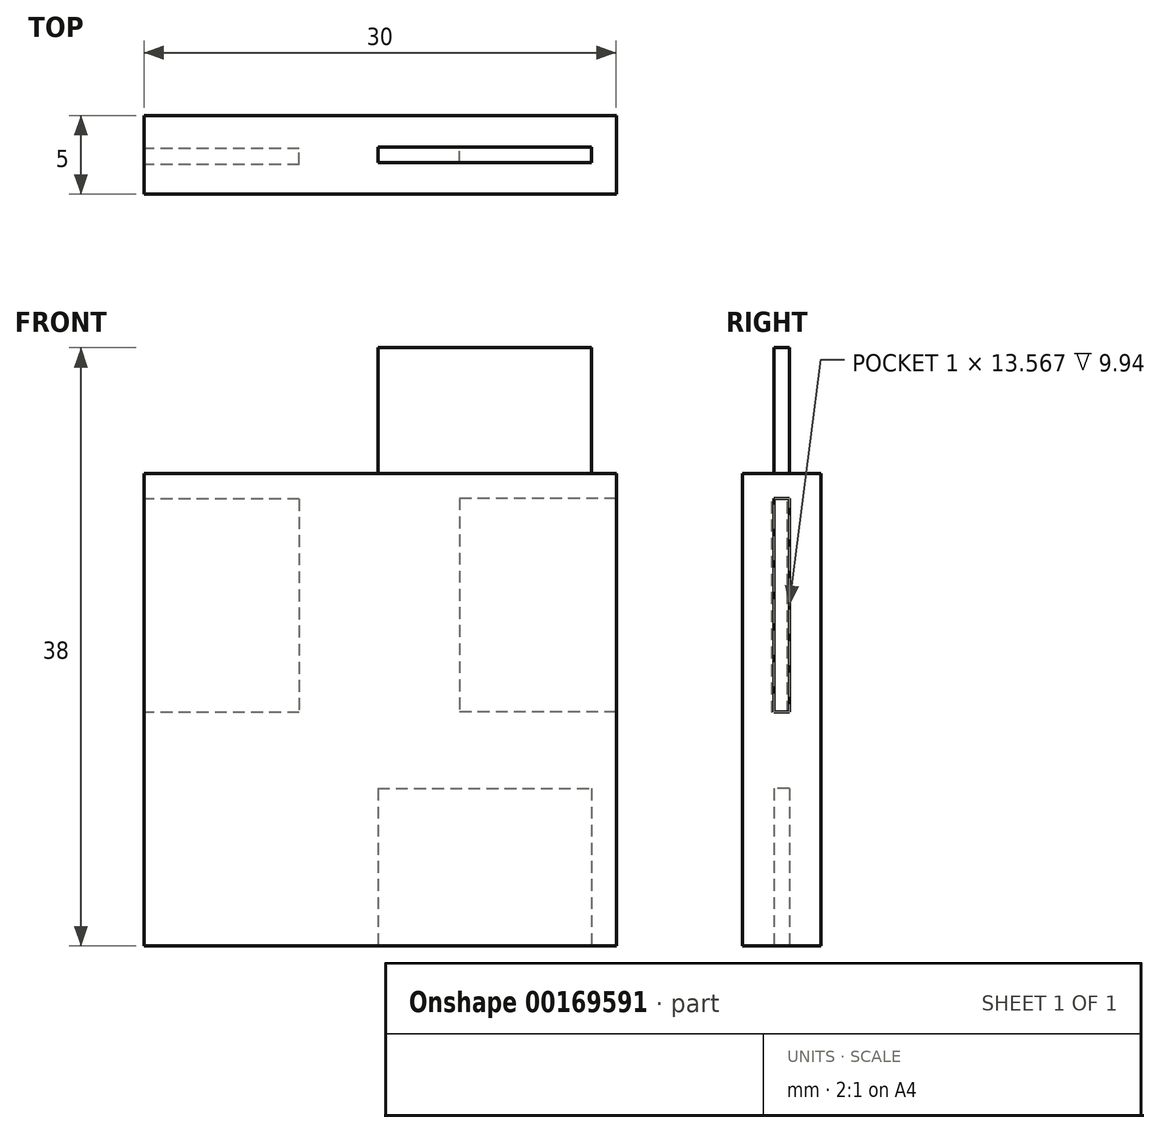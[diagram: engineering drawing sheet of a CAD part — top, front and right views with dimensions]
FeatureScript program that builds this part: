
annotation { "Feature Type Name" : "Feature", "Feature Type Description" : "" }
export const myFeature = defineFeature(function(context is Context, id is Id, definition is map)
    precondition{}
    {
        {
            var Q0;
            Q0=qCreatedBy(makeId("Top.planeOp"),FACE);
            var sketch = newSketch(context, id + "F0", { "sketchPlane" : qUnion([Q0])});
            skLineSegment(sketch, "E0.bottom", {"start": v(-14.86, -2.76) * mm, "end": v(15.14, -2.76) * mm});
            skLineSegment(sketch, "E0.top", {"start": v(-14.86, -7.76) * mm, "end": v(15.14, -7.76) * mm});
            skLineSegment(sketch, "E0.left", {"start": v(-14.86, -2.76) * mm, "end": v(-14.86, -7.76) * mm});
            skLineSegment(sketch, "E0.right", {"start": v(15.14, -2.76) * mm, "end": v(15.14, -7.76) * mm});
            skSolve(sketch);
        }
        {
            var Q0;
            Q0 = qSketchRegion(id + "F0", true);
            extrude(context, id + "F1", {"entities" : qUnion([Q0]), "depth" : 30 * mm, "offsetDistance" : 25 * mm});
        }
        {
            var Q0;
            Q0=qCreatedBy(makeId("Top.planeOp"),FACE);
            var sketch = newSketch(context, id + "F2", { "sketchPlane" : qUnion([Q0])});
            skLineSegment(sketch, "E1.bottom", {"start": v(0, -4.76) * mm, "end": v(13.57, -4.76) * mm});
            skLineSegment(sketch, "E1.top", {"start": v(0, -5.76) * mm, "end": v(13.57, -5.76) * mm});
            skLineSegment(sketch, "E1.left", {"start": v(0, -4.76) * mm, "end": v(0, -5.76) * mm});
            skLineSegment(sketch, "E1.right", {"start": v(13.57, -4.76) * mm, "end": v(13.57, -5.76) * mm});
            skSolve(sketch);
        }
        {
            var Q0;
            Q0 = qSketchRegion(id + "F2", true);
            extrude(context, id + "F3", {"entities" : qUnion([Q0]), "operationType" : NewBodyOperationType.REMOVE, "depth" : 10 * mm, "offsetDistance" : 25 * mm});
        }
        {
            var Q0;
            Q0=qCreatedBy(makeId("Top.planeOp"),FACE);
            var sketch = newSketch(context, id + "F4", { "sketchPlane" : qUnion([Q0])});
            skLineSegment(sketch, "E2.bottom", {"start": v(0, -4.76) * mm, "end": v(13.57, -4.76) * mm});
            skLineSegment(sketch, "E2.top", {"start": v(0, -5.76) * mm, "end": v(13.57, -5.76) * mm});
            skLineSegment(sketch, "E2.left", {"start": v(0, -4.76) * mm, "end": v(0, -5.76) * mm});
            skLineSegment(sketch, "E2.right", {"start": v(13.57, -4.76) * mm, "end": v(13.57, -5.76) * mm});
            skSolve(sketch);
        }
        {
            var Q0;
            Q0 = qSketchRegion(id + "F4", true);
            extrude(context, id + "F5", {"entities" : qUnion([Q0]), "depth" : 8 * mm, "offsetDistance" : 25 * mm});
        }
        {
            var Q0;
            Q0=makeQuery(id+"F5.opExtrude","SWEPT_BODY",BODY,{"disambiguationData":[OSD([sQuery(id+"F4.wireOp",EDGE,"E2.bottom"),sQuery(id+"F4.wireOp",EDGE,"E2.top"),sQuery(id+"F4.wireOp",EDGE,"E2.left"),sQuery(id+"F4.wireOp",EDGE,"E2.right")])]});
            transform(context, id + "F6", {"entities" : qUnion([Q0]), "transformType" : TransformType.TRANSLATION_3D, "dx" : 0 * mm, "dy" : 0 * mm, "dz" : 30 * mm, "makeCopy" : false});
        }
        {
            var Q0;
            Q0=qCreatedBy(makeId("Right.planeOp"),FACE);
            var sketch = newSketch(context, id + "F7", { "sketchPlane" : qUnion([Q0])});
            skLineSegment(sketch, "E3.bottom", {"start": v(-5.87, 31.97) * mm, "end": v(-4.87, 31.97) * mm});
            skLineSegment(sketch, "E3.top", {"start": v(-5.87, 18.4) * mm, "end": v(-4.87, 18.4) * mm});
            skLineSegment(sketch, "E3.left", {"start": v(-5.87, 31.97) * mm, "end": v(-5.87, 18.4) * mm});
            skLineSegment(sketch, "E3.right", {"start": v(-4.87, 31.97) * mm, "end": v(-4.87, 18.4) * mm});
            skSolve(sketch);
        }
        {
            var Q0;
            Q0 = qSketchRegion(id + "F7", true);
            extrude(context, id + "F8", {"entities" : qUnion([Q0]), "depth" : 10 * mm, "offsetDistance" : 25 * mm});
        }
        {
            var Q0;
            Q0=makeQuery(id+"F8.opExtrude","SWEPT_BODY",BODY,{"disambiguationData":[OSD([sQuery(id+"F7.wireOp",EDGE,"E3.bottom"),sQuery(id+"F7.wireOp",EDGE,"E3.top"),sQuery(id+"F7.wireOp",EDGE,"E3.left"),sQuery(id+"F7.wireOp",EDGE,"E3.right")])]});
            transform(context, id + "F9", {"entities" : qUnion([Q0]), "transformType" : TransformType.TRANSLATION_3D, "dx" : -15 * mm, "dy" : 0 * mm, "dz" : -3.57 * mm, "makeCopy" : false});
        }
        {
            var Q0;
            Q0=makeQuery(id+"F8.opExtrude","SWEPT_BODY",BODY,{"disambiguationData":[OSD([sQuery(id+"F7.wireOp",EDGE,"E3.bottom"),sQuery(id+"F7.wireOp",EDGE,"E3.top"),sQuery(id+"F7.wireOp",EDGE,"E3.left"),sQuery(id+"F7.wireOp",EDGE,"E3.right")])]});
            var Q1;
            Q1=makeQuery(id+"F1.opExtrude","SWEPT_BODY",BODY,{"disambiguationData":[OSD([sQuery(id+"F0.wireOp",EDGE,"E0.bottom"),sQuery(id+"F0.wireOp",EDGE,"E0.top"),sQuery(id+"F0.wireOp",EDGE,"E0.left"),sQuery(id+"F0.wireOp",EDGE,"E0.right")])]});
            booleanBodies(context, id + "F10", {"operationType" : BooleanOperationType.SUBTRACTION, "tools" : qUnion([Q0]), "targets" : qUnion([Q1])});
        }
        {
            var Q0;
            Q0=qCreatedBy(makeId("Right.planeOp"),FACE);
            var sketch = newSketch(context, id + "F11", { "sketchPlane" : qUnion([Q0])});
            skLineSegment(sketch, "E4.bottom", {"start": v(-5.76, 28.43) * mm, "end": v(-4.76, 28.43) * mm});
            skLineSegment(sketch, "E4.top", {"start": v(-5.76, 14.86) * mm, "end": v(-4.76, 14.86) * mm});
            skLineSegment(sketch, "E4.left", {"start": v(-5.76, 28.43) * mm, "end": v(-5.76, 14.86) * mm});
            skLineSegment(sketch, "E4.right", {"start": v(-4.76, 28.43) * mm, "end": v(-4.76, 14.86) * mm});
            skSolve(sketch);
        }
        {
            var Q0;
            Q0 = qSketchRegion(id + "F11", true);
            extrude(context, id + "F12", {"entities" : qUnion([Q0]), "depth" : 10 * mm, "offsetDistance" : 25 * mm});
        }
        {
            var Q0;
            Q0=makeQuery(id+"F12.opExtrude","SWEPT_BODY",BODY,{"disambiguationData":[OSD([sQuery(id+"F11.wireOp",EDGE,"E4.bottom"),sQuery(id+"F11.wireOp",EDGE,"E4.top"),sQuery(id+"F11.wireOp",EDGE,"E4.left"),sQuery(id+"F11.wireOp",EDGE,"E4.right")])]});
            transform(context, id + "F13", {"entities" : qUnion([Q0]), "transformType" : TransformType.TRANSLATION_3D, "dx" : 5.2 * mm, "dy" : 0 * mm, "dz" : 0 * mm, "makeCopy" : false});
        }
        {
            var Q0;
            Q0=makeQuery(id+"F12.opExtrude","SWEPT_BODY",BODY,{"disambiguationData":[OSD([sQuery(id+"F11.wireOp",EDGE,"E4.bottom"),sQuery(id+"F11.wireOp",EDGE,"E4.top"),sQuery(id+"F11.wireOp",EDGE,"E4.left"),sQuery(id+"F11.wireOp",EDGE,"E4.right")])]});
            var Q1;
            Q1=makeQuery(id+"F1.opExtrude","SWEPT_BODY",BODY,{"disambiguationData":[OSD([sQuery(id+"F0.wireOp",EDGE,"E0.bottom"),sQuery(id+"F0.wireOp",EDGE,"E0.top"),sQuery(id+"F0.wireOp",EDGE,"E0.left"),sQuery(id+"F0.wireOp",EDGE,"E0.right")])]});
            booleanBodies(context, id + "F14", {"operationType" : BooleanOperationType.SUBTRACTION, "tools" : qUnion([Q0]), "targets" : qUnion([Q1])});
        }
    });
